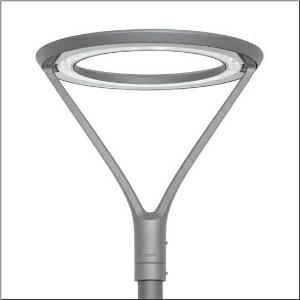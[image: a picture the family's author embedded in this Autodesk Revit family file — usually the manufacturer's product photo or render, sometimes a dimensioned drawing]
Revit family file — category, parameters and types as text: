
# Revit family: dl_r__20___pl1_2s_5xa51283ws008p_a586
name_source: partatom
category: Lighting Fixtures
units: mm (PartAtom-declared; Revit-internal decimal feet)

## family parameters
Cut with Voids When Loaded = No
Host = Face
Light Source = No
Part Type = Normal
Room Calculation Point = No
Round Connector Dimension = Use Diameter
Shared = No

## types (1)
- --- (1 x LED, 4250 lm, 34.3 W, 3000K)
    Apparent Load = 34 VA
    CIE Flux Codes = 33 78 99 100 100
    Color Rendering = 70
    Color Temperature = 3000K
    Default Elevation = 1800 mm
    Description = DL® 20, mast luminaire, primary light control with reflector, highly specular, primary optical cover: cover, of toughened safety glass of clear glass with excellent transmission level, light distribution: PL1.2s, light emission: direct distribution, primary light characteristic: symmetric, installation type: post-top, LED, High Power LED, rated luminous flux: 4.210lm, luminous efficacy: 80lm/W, light colour: 730, colour temperature: 3000K, control gear: Plus, control: overheat protection, power reduction, digital communication interface, constant luminous flux control, time-dependent luminous flux control, flexible luminous flux parameterisation, electronic power reduction, mains connection: 230..240V, 50/60Hz, connection cable pre-assembled, cable length: 5m, start of lifetime: 53W, end of service life: 54W, reduction: 24W, luminaire housing, upper part, of cast aluminium, powder-coated, Siteco® metallic grey (DB 702S), diameter: 690mm, height: 690mm, spigot size: 76mm (post-top), mounting height: 4..6m, luminaire housing, of cast aluminium, powder-coated, Siteco® metallic grey (DB 702S), equipment: Power, protection rating (complete): IP66, insulation class (complete): insulation class II (safety insulation), certification: CE, ENEC, VDE, impact resistance: IK08, permissible operating ambient temperature: -25..+30°C, standard-compliant lighting for roads and squares, packaging unit: 1 piece

Light Distribution: PL1.2s
    Height = 690 mm
    Lamp = 1 x LED
    Lamp Light Flux = 4250 lm
    Lamp Power = 34.3 W
    Lamp count = 1
    Length = 690 mm
    Luminous efficacy = 124 lm/W
    Manufacturer = Siteco
    ModVariant = No
    Model = 5XA51283WS008P
    Number of Poles = 1
    OnlyDefault = Yes
    Power Factor = 1
    Product Name = DL® 20 | PL1.2s
    Product group = mast luminaire | pylon top
    ProductGroupID = 6100
    Protection Class = Protection class II
    Protection Degree = IP 66
    RLX_Detail_Level = 1
    RLX_Emergency_Light_Flux = 0 lm
    RLX_Emergency_Type = 0
    RLX_Emergency_Type_DB = No
    RlxData = <blob elided: 204873 chars, md5=3d4677a9>
    Socket = socket
    Standby Power = 0 W
    System Light Flux = 4250 lm
    System Power = 34 W
    Type Comments = factory setting: luminous flux: 100 % | dim-lin: 254 | 464 mA
    Type Image = l_1006001.jpg
    URL = http://relux.com
    VarID = @adj_098419
    Voltage = 0 V
    Weight = 0.00 kg
    Width = 0 mm  [stored 0 ft]

note: [stored X ft] marks values corroborated as IEEE doubles in the binary element streams (Revit-internal decimal feet)

## geometry (parser evidence)
native form markers: Blend x4, Sweep x11
no freeform markers — native parametric forms only
